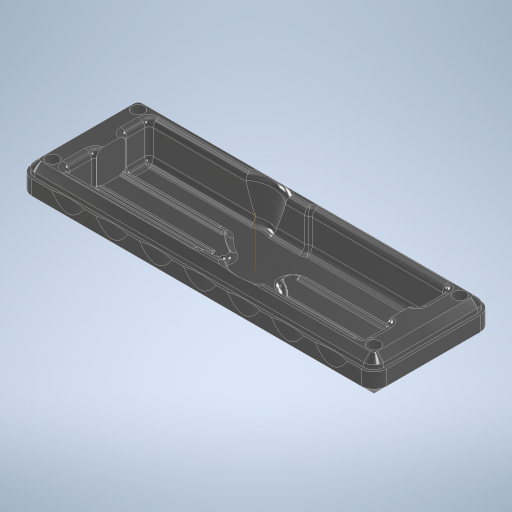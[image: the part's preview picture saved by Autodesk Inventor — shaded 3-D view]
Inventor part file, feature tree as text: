
AUTODESK INVENTOR PART (.ipt)
format: ipt  version: 2024.1 (Build 281209000, 209)  size: 2,560,000 bytes
history: native  units: mm
features: projected_geometry x33, extrude x24, fillet x18, sketch x6, chamfer x5, other x4, pattern_circular x2, plane x1, pattern_linear x1, mirror x1
ambient origin geometry x8: Origin, YZ Plane, XZ Plane, XY Plane, X Axis, Y Axis, Z Axis, Center Point
bodies: Body1 (feature_tree), Body2 (feature_tree), Body3 (feature_tree)
feature tree (95):
  other  "case"
  extrude  "Extrusion1"  Depth=56.0mm
  extrude  "Extrusion2"  Depth=28.0mm
  extrude  "Extrusion3"  Depth=2.0mm
  fillet  "Fillet1"  Radius=4.0mm
  fillet  "Fillet2"  Radius=20.0mm
  fillet  "Fillet3"  Radius=4.0mm
  pattern_circular  "Circular Pattern1"  Count=2  [1 undecoded]
  fillet  "Fillet4"  Radius=96.0mm
  chamfer  "Chamfer1"  Distance=14.3mm
  extrude  "Extrusion4"  Depth=12.4mm
  chamfer  "Chamfer2"  Distance=0.95mm
  extrude  "Extrusion5"  Depth=0.95mm
  pattern_circular  "Circular Pattern2"  [2 undecoded]
  fillet  "Fillet5"  Radius=3.7mm
  fillet  "Fillet6"  Radius=17.6mm
  fillet  "Fillet10"  Radius=25.0mm
  fillet  "Fillet11"  Radius=16.6mm
  fillet  "Fillet12"  Radius=4.0mm
  extrude  "Extrusion6"  Depth=3.0mm
  plane  "Work Plane1"
  extrude  "Extrusion7"  Depth=4.0mm
  extrude  "Extrusion8"  Depth=20.0mm TaperAngle=180.0deg
  extrude  "Extrusion9"  Depth=6.0mm
  fillet  "Fillet8"  Radius=6.0mm
  extrude  "Extrusion10"  Depth=1.3mm
  pattern_linear  "Rectangular Pattern1"  Spacing1=5.0mm  [1 undecoded]
  mirror  "Mirror1"
  extrude  "Extrusion11"  Depth=3.0mm TaperAngle=45.0deg
  extrude  "Extrusion15"  Depth=6.0mm
  extrude  "Extrusion16"  Depth=6.5mm
  chamfer  "Chamfer4"  Distance=6.5mm
  extrude  "Extrusion18"  Depth=22.0mm
  extrude  "Extrusion19"  Depth=2.0mm TaperAngle=0.0deg
  extrude  "Extrusion12"  Depth=20.0mm TaperAngle=360.0deg
  extrude  "Extrusion13"  Depth=6.5mm
  extrude  "Extrusion14"  Depth=6.5mm
  extrude  "Extrusion17"  Depth=2.0mm
  chamfer  "Chamfer5"  Distance=3.0mm
  chamfer  "Chamfer6"  Distance=6.5mm
  extrude  "Extrusion20"  Depth=6.45mm
  fillet  "Fillet13"  Radius=1.0mm
  extrude  "Extrusion21"  Depth=3.0mm TaperAngle=0.0deg
  extrude  "Extrusion22"  Depth=3.1mm TaperAngle=0.0deg
  extrude  "Extrusion23"  Depth=1.8mm TaperAngle=0.0deg
  fillet  "Fillet15"  Radius=0.5mm
  fillet  "Fillet16"  Radius=1.0mm
  fillet  "Fillet17"  Radius=0.5mm
  fillet  "Fillet18"  Radius=60.0mm
  fillet  "Fillet19"  Radius=20.0mm
  fillet  "Fillet20"  Radius=29.0mm
  extrude  "Extrusion24"  Depth=8.5mm
  fillet  "Fillet14"  Radius=70.0mm
  projected_geometry  "Projected Loop1"
  projected_geometry  "Projected Loop5"
  other  "Work Axis1"
  projected_geometry  "Projected Loop7"
  other  "lid"
  projected_geometry  "Projected Loop8"
  projected_geometry  "Projected Loop9"
  projected_geometry  "Projected Loop10"
  projected_geometry  "Projected Loop11"
  sketch  "Sketch15"  dims[d0=167.0mm d1=56.0mm]
  sketch  "Sketch16"  dims[d2=83.5mm d3=28.0mm]
  other  "lid-part2"
  projected_geometry  "Projected Loop12"
  projected_geometry  "Projected Loop13"
  projected_geometry  "Projected Loop14"
  projected_geometry  "Projected Loop15"
  projected_geometry  "Projected Loop16"
  projected_geometry  "Projected Loop17"
  projected_geometry  "Projected Loop18"
  projected_geometry  "Projected Loop19"
  projected_geometry  "Projected Loop20"
  projected_geometry  "Projected Loop21"
  projected_geometry  "Projected Loop22"
  projected_geometry  "Projected Loop23"
  projected_geometry  "Projected Loop24"
  projected_geometry  "Projected Loop25"
  projected_geometry  "Projected Loop26"
  projected_geometry  "Projected Loop27"
  projected_geometry  "Projected Loop28"
  projected_geometry  "Projected Loop29"
  projected_geometry  "Projected Loop30"
  projected_geometry  "Projected Loop31"
  projected_geometry  "Projected Loop32"
  projected_geometry  "Projected Loop33"
  sketch  "Sketch24"  dims[d4=18.0mm d5=0.0mm d6=2.0mm d8=4.0mm d9=20.0mm d10=4.0mm d11=20.0mm d12=96.0mm]
  sketch  "Sketch25"  dims[d13=65.0mm]
  sketch  "Sketch26"  dims[d14=74.2mm]
  sketch  "Sketch27"  dims[d15=12.0mm d16=14.3mm d17=12.4mm d18=0.95mm d19=0.95mm d20=2.0mm d21=3.7mm d22=17.6mm d23=0.0mm d24=25.0mm d27=16.6mm d28=-1.745329mm d29=4.0mm d30=3.0mm d31=4.0mm d32=20.0mm d33=180.0deg d35=6.0mm d36=6.0mm d37=2.0mm d38=45.0deg d39=1.3mm d40=5.0mm d41=0.0mm d42=3.0mm d43=2.0mm d44=45.0deg d45=6.0mm d46=6.5mm d47=6.5mm d48=22.0mm d49=2.0mm d50=0.0mm d51=20.0mm d52=360.0deg d54=6.5mm d55=6.5mm d56=2.0mm d57=3.0mm d59=6.5mm d60=6.45mm d61=1.0mm d62=3.0mm d63=0.0mm d64=3.1mm d65=0.0mm d69=1.8mm d70=0.0mm d71=0.5mm d72=1.0mm d73=0.0mm d74=0.5mm d75=60.0mm d76=20.0mm d77=29.0mm d79=8.5mm d80=-1.745329mm d82=70.0mm d84=124.0mm d85=55.0mm d86=1.0mm d89=0.06mm d90=0.0mm d91=0.02mm d92=0.0mm d93=30.0deg d94=1.0mm d95=6.0mm d96=6.0mm d97=7.0mm d98=6.0mm d99=6.0mm d101=1.0mm d108=3.0mm d109=3.0mm d110=0.04mm d111=0.0mm d112=1.6mm d113=1.6mm d114=1.1mm d115=1.1mm d116=7.0mm d117=3.0mm d119=2.0mm d120=1.1mm d121=1.1mm d122=1.5mm d123=1.5mm d124=1.5mm d125=1.0mm d126=1.1mm d127=1.1mm d128=1.8mm d131=2.0mm d132=1.5mm d133=1.5mm d140=50.0mm d142=8.0mm d143=60.0mm d145=8.0mm d148=0.0mm d149=0.0mm d150=0.0mm d151=0.0mm d152=3.5mm d153=0.0mm d154=2.5mm d155=2.0mm d156=45.0deg d158=0.4mm d159=0.4mm d160=0.0mm d163=3.0mm d164=1.5mm d165=0.4mm d166=0.0mm d167=3.1mm d168=0.0mm d169=1.5mm d170=2.0mm d171=45.0deg d172=1.5mm d173=2.0mm d174=45.0deg d175=8.0mm d176=8.0mm d177=45.0mm d178=16.0mm d179=3.0mm d180=3.0mm d181=3.0mm d182=0.0mm d183=0.0mm d184=1.0mm d185=137.3mm d186=10.5mm d187=10.6mm d188=12.55mm d189=6.275mm d190=15.5mm d191=0.0mm d192=14.0mm d193=0.0mm d194=2.0mm d195=0.675mm d196=0.675mm d197=0.675mm d198=14.0mm d199=0.0mm d200=2.0mm d201=0.6mm d202=0.6mm d203=0.3mm d204=0.3mm d205=0.3mm d206=12.0mm d207=0.0mm]
  projected_geometry  "Projected Loop34"
  projected_geometry  "Projected Loop35"
  projected_geometry  "Projected Loop36"
  projected_geometry  "Projected Loop37"
note: 4 required parameter values undecoded (feature->parameter linkage not recoverable at this tier; creation-order binding heuristic only, values carry confidence <= 0.55)
